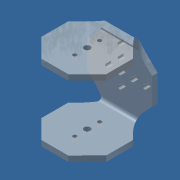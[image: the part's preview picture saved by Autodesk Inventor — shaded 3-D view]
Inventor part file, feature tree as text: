
AUTODESK INVENTOR PART (.ipt)
format: ipt  version: 2014 (Build 180170000, 170)  size: 224,256 bytes
history: native  units: in
note: dims shown in document units (in); Inventor stores cm internally (conversion verified against a paired STEP export)
features: extrude x6, sketch x6, plane x2, fillet x2, mirror x2
ambient origin geometry x8: Origin, YZ Plane, XZ Plane, XY Plane, X Axis, Y Axis, Z Axis, Center Point
bodies: Solid1 (feature_tree)
feature tree (18):
  extrude  "Extrusion1"  TaperAngle=0.0deg  [1 undecoded]
  extrude  "Extrusion2"  Depth=0.1772in
  plane  "Work Plane1"
  extrude  "Extrusion3"  Depth=0.1772in
  fillet  "Fillet1"  [1 undecoded]
  plane  "Work Plane2"
  mirror  "Mirror1"
  fillet  "Fillet2"  Radius=0.1181in
  extrude  "Extrusion4"  Depth=0.5906in
  extrude  "Extrusion5"  Depth=0.1772in
  extrude  "Extrusion7"  Depth=0.3937in
  mirror  "Mirror2"
  sketch  "Sketch1"  dims[d0=2.0472in d3=0.0in]
  sketch  "Sketch2"  dims[d4=2.0472in d5=0.1772in]
  sketch  "Sketch3"  dims[d6=0.0in d7=0.1772in d8=0.0in d9=0.1181in]
  sketch  "Sketch4"  dims[d10=-1.0236in d11=0.5906in]
  sketch  "Sketch5"  dims[d12=0.1969in d15=0.1772in]
  sketch  "Sketch7"  dims[d16=0.0in d17=0.1181in d18=0.1181in d19=0.3937in d20=0.1181in d21=0.3937in d22=0.1181in d23=0.1181in d24=0.3937in d25=0.3937in d26=0.1181in d27=0.0in d35=0.1181in d36=0.3937in d37=0.1181in d38=0.3937in d39=0.0in d40=0.0in d41=0.1181in d42=0.2559in d43=0.3937in d45=0.1181in d46=0.2559in d47=0.3937in]
note: 2 required parameter values undecoded (feature->parameter linkage not recoverable at this tier; creation-order binding heuristic only, values carry confidence <= 0.55)
